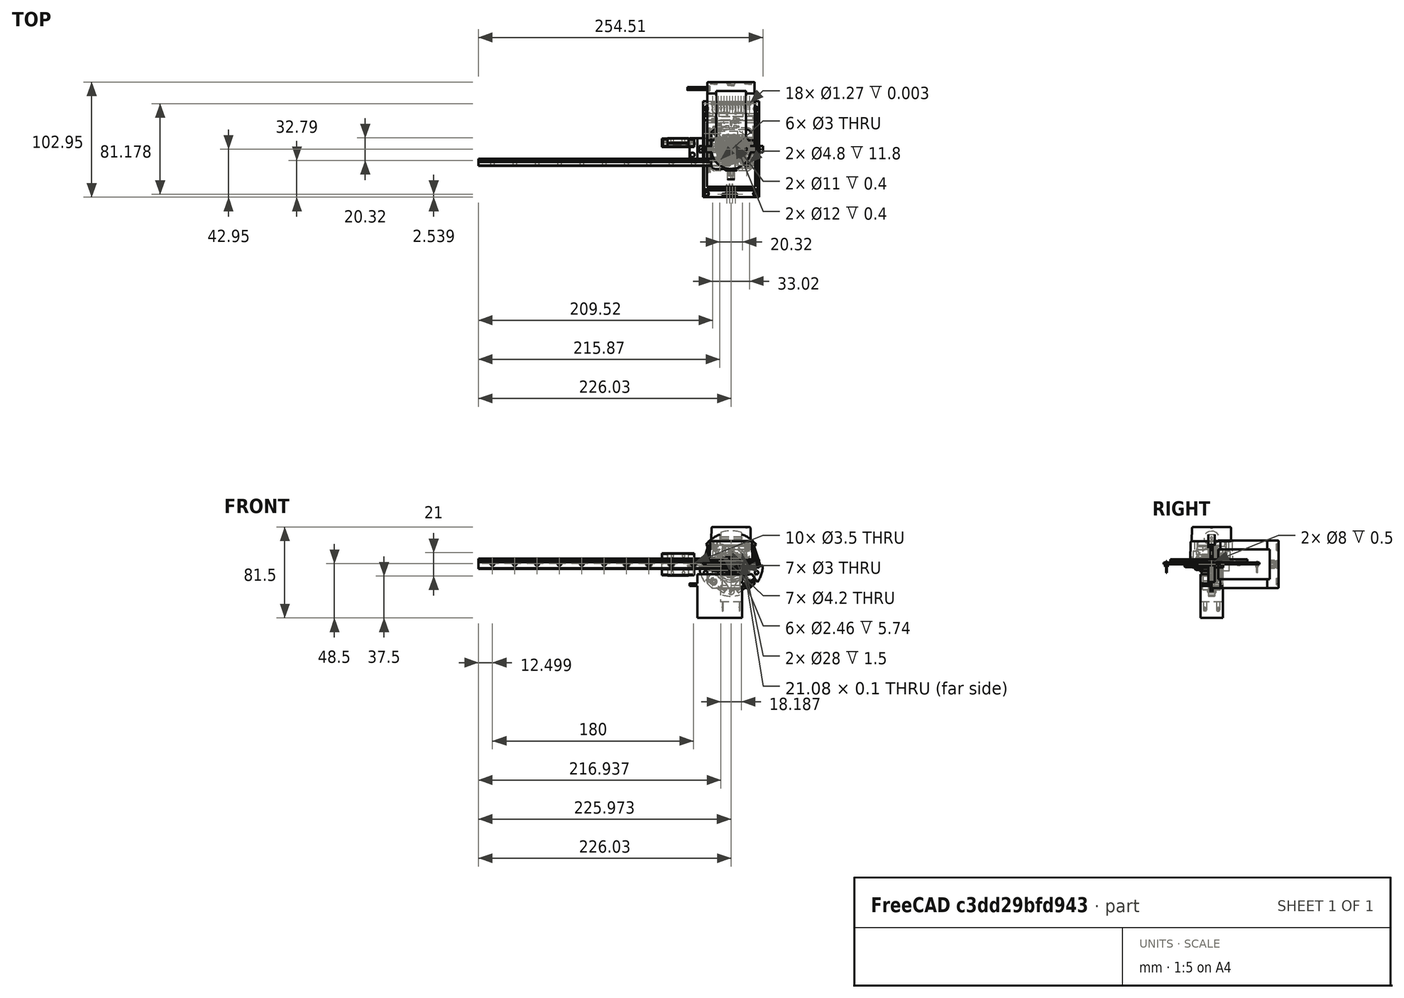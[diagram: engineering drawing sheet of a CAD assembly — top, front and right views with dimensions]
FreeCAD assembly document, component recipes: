
FREECAD ASSEMBLY — COMPONENT RECIPES ("generic-hardware")

This assembly document has 34 components, labeled P0..P33 below (a component is one placed body or linked part). 32 of them carry a construction recipe — the FreeCAD feature program that regenerates the part from scratch, quoted from this document or its linked companion documents; the rest are supplied as boundary geometry only. No exploded tour is included for this assembly.
NOTE — document 3 of 3 of this assembly tour. The two overview renders and the header above are repeated from document 1; the component sections below continue where the previous document stopped.
COMPONENT P32 — recipe-attached ("BAU-LBM4-16mm", modeled in this document).
Construction recipe (the document's own serialized feature program — sketch geometry with constraints, then the solid features built on it; lengths are millimeters unless a unit is written):

FEATURE [Sketcher::SketchObject] Sketch251
  ArcFitTolerance = 1e-06
  AttachmentSupport = -> [XZ_Plane143]
  ExternalBSplineMaxDegree = 5
  ExternalBSplineTolerance = 0.0001
  FullyConstrained = true
  InternalTolerance = 1e-06
  InvalidShape = false
  MakeInternals = false
  MapMode = 5
  Placement = pos=(0,0,0) rot=(1,0,0;1.5708rad)
  Support = -> [XZ_Plane143]
  TreeRank = 77
  ValidateShape = false
  sketch-geometry (8):
    g0: LineSegment StartX=0 StartY=6.5 StartZ=0 EndX=10.75 EndY=6.5 EndZ=0
    g1: LineSegment StartX=10.75 StartY=6.5 StartZ=0 EndX=10.75 EndY=1.5 EndZ=0
    g2: LineSegment StartX=10.75 StartY=1.5 StartZ=0 EndX=11.75 EndY=1.5 EndZ=0
    g3: LineSegment StartX=11.75 StartY=1.5 StartZ=0 EndX=11.75 EndY=0 EndZ=0
    g4: LineSegment StartX=11.75 StartY=0 StartZ=0 EndX=8 EndY=0 EndZ=0
    g5: LineSegment StartX=8 StartY=0 StartZ=0 EndX=8 EndY=-15 EndZ=0
    g6: LineSegment StartX=8 StartY=-15 StartZ=0 EndX=0 EndY=-15 EndZ=0
    g7: LineSegment StartX=0 StartY=-15 StartZ=0 EndX=0 EndY=6.5 EndZ=0
  constraints (24):
    c: PointOnObject(g0,g-2)
    c: Horizontal(g0)
    c: Coincident(g0,g1)
    c: Coincident(g1,g2)
    c: Horizontal(g2)
    c: Coincident(g2,g3)
    c: Vertical(g3)
    c: Coincident(g3,g4)
    c: Horizontal(g4)
    c: Coincident(g4,g5)
    c: Vertical(g5)
    c: Coincident(g5,g6)
    c: Horizontal(g6)
    c: Coincident(g6,g7)
    c: Coincident(g7,g0)
    c: Vertical(g7)
    c: Vertical(g1)
    c: PointOnObject(g4,g-1)
    c: DistanceX(g6,g6) = 8
    c: DistanceX(g3) = 11.75
    c: DistanceY(g3,g3) = 1.5
    c: DistanceX(g1) = 10.75
    c: DistanceY(g1,g1) = 5
    c: DistanceY(g5,g5) = 15
FEATURE [PartDesign::Revolution] Revolution
  AddSubType = 0
  Angle = 360
  Axis = (0,2e-16,1)
  Base = (0,0,0)
  ClaimChildren = false
  Fit = 0
  FitJoin = 0
  InnerFit = 0
  InnerFitJoin = 0
  InvalidShape = false
  Linearize = true
  NewSolid = false
  Profile = -> Sketch251
  ReferenceAxis = -> Sketch251 [V_Axis]
  Refine = true
  Reversed = true
  Suppress = false
  TreeRank = 78
  ValidateShape = true
  _ProfileBasedVersion = 1
FEATURE [PartDesign::Body] Body117  label="LBM4-16mm-Body"
  AutoGroupSolids = false
  ClaimAllChildren = false
  ExportMode = 0
  Group = -> [Sketch251,Revolution]
  InvalidShape = false
  Origin = -> Origin221
  Tip = -> Revolution
  TreeRank = 76
  ValidateShape = false
  _ExportChildren = -> [Revolution]
  _GroupVersion = 1
FEATURE [Sketcher::SketchObject] Sketch252
  ArcFitTolerance = 1e-06
  AttachmentSupport = -> [XZ_Plane144]
  ExternalBSplineMaxDegree = 5
  ExternalBSplineTolerance = 0.0001
  FullyConstrained = true
  InternalTolerance = 1e-06
  InvalidShape = false
  MakeInternals = false
  MapMode = 5
  Placement = pos=(0,0,0) rot=(1,0,0;1.5708rad)
  Support = -> [XZ_Plane144]
  TreeRank = 89
  ValidateShape = false
  sketch-geometry (8):
    g0: LineSegment StartX=0 StartY=10.5 StartZ=0 EndX=13 EndY=10.5 EndZ=0
    g1: LineSegment StartX=13 StartY=10.5 StartZ=0 EndX=13 EndY=8 EndZ=0
    g2: LineSegment StartX=13 StartY=8 StartZ=0 EndX=13.5 EndY=8 EndZ=0
    g3: LineSegment StartX=13.5 StartY=8 StartZ=0 EndX=13.5 EndY=3 EndZ=0
    g4: LineSegment StartX=13.5 StartY=3 StartZ=0 EndX=12.75 EndY=3 EndZ=0
    g5: LineSegment StartX=12.75 StartY=3 StartZ=0 EndX=12.75 EndY=0 EndZ=0
    g6: LineSegment StartX=12.75 StartY=0 StartZ=0 EndX=0 EndY=0 EndZ=0
    g7: LineSegment StartX=0 StartY=0 StartZ=0 EndX=0 EndY=10.5 EndZ=0
  constraints (23):
    c: PointOnObject(g0,g-2)
    c: Horizontal(g0)
    c: Coincident(g0,g1)
    c: Vertical(g1)
    c: Coincident(g1,g2)
    c: Horizontal(g2)
    c: Coincident(g2,g3)
    c: Vertical(g3)
    c: Coincident(g3,g4)
    c: Horizontal(g4)
    c: Coincident(g4,g5)
    c: PointOnObject(g5,g-1)
    c: Vertical(g5)
    c: Coincident(g5,g6)
    c: Coincident(g6,g-1)
    c: Coincident(g6,g7)
    c: Coincident(g7,g0)
    c: DistanceY(g3,g3) = 5
    c: DistanceX(g0,g0) = 13
    c: DistanceX(g2) = 13.5
    c: DistanceY(g7,g7) = 10.5
    c: DistanceY(g5,g5) = 3
    c: DistanceX(g6,g6) = 12.75
FEATURE [PartDesign::Revolution] Revolution022
  AddSubType = 0
  Angle = 360
  Axis = (0,2e-16,1)
  Base = (0,0,0)
  ClaimChildren = false
  Fit = 0
  FitJoin = 0
  InnerFit = 0
  InnerFitJoin = 0
  InvalidShape = false
  Linearize = true
  NewSolid = false
  Profile = -> Sketch252
  ReferenceAxis = -> Sketch252 [V_Axis]
  Refine = true
  Reversed = true
  Suppress = false
  TreeRank = 90
  ValidateShape = true
  _ProfileBasedVersion = 1
FEATURE [PartDesign::Fillet] Fillet049
  AddSubType = 0
  Base = -> Revolution022 [Edge1]
  BaseFeature = -> Revolution022
  InvalidShape = false
  NewSolid = false
  Radius = 2
  Refine = true
  SupportTransform = false
  Suppress = false
  TreeRank = 91
  UseAllEdges = false
  ValidateShape = true
FEATURE [PartDesign::Chamfer] Chamfer058
  AddSubType = 0
  Angle = 45
  Base = -> Fillet049 [Edge6,Edge8]
  BaseFeature = -> Fillet049
  ChamferType = 0
  FlipDirection = false
  InvalidShape = false
  NewSolid = false
  Refine = true
  Size = 0.4
  Size2 = 1
  SupportTransform = false
  Suppress = false
  TreeRank = 92
  UseAllEdges = false
  ValidateShape = true
FEATURE [PartDesign::Fillet] Fillet050
  AddSubType = 0
  Base = -> Chamfer058 [Edge15]
  BaseFeature = -> Chamfer058
  InvalidShape = false
  NewSolid = false
  Radius = 0.2
  Refine = true
  SupportTransform = false
  Suppress = false
  TreeRank = 93
  UseAllEdges = false
  ValidateShape = true
FEATURE [PartDesign::Body] Body118  label="LBM4-Button"
  AutoGroupSolids = false
  ClaimAllChildren = false
  ExportMode = 0
  Group = -> [Sketch252,Revolution022,Fillet049,Chamfer058,Fillet050]
  InvalidShape = false
  Origin = -> Origin222
  Placement = pos=(0,0,5.5) rot=(0,0,1;0rad)
  Tip = -> Fillet050
  TreeRank = 88
  ValidateShape = false
  _ExportChildren = -> [Revolution022,Fillet049,Chamfer058,Fillet050]
  _GroupVersion = 1
FEATURE [Sketcher::SketchObject] Sketch253
  ArcFitTolerance = 1e-06
  AttachmentSupport = -> [XZ_Plane145]
  ExternalBSplineMaxDegree = 5
  ExternalBSplineTolerance = 0.0001
  FullyConstrained = true
  InternalTolerance = 1e-06
  InvalidShape = false
  MakeInternals = false
  MapMode = 5
  Placement = pos=(0,0,0) rot=(1,0,0;1.5708rad)
  Support = -> [XZ_Plane145]
  TreeRank = 104
  ValidateShape = false
  sketch-geometry (1):
    g0: Circle CenterX=8.5 CenterY=0 CenterZ=0 NormalX=0 NormalY=0 NormalZ=1 AngleXU=0 Radius=0.75
  constraints (3):
    c: PointOnObject(g0,g-1)
    c: Diameter(g0) = 1.5
    c: DistanceX(g0) = 8.5
FEATURE [PartDesign::Revolution] Revolution023
  AddSubType = 0
  Angle = 360
  Axis = (0,2e-16,1)
  Base = (0,0,0)
  ClaimChildren = false
  Fit = 0
  FitJoin = 0
  InnerFit = 0
  InnerFitJoin = 0
  InvalidShape = false
  Linearize = true
  NewSolid = false
  Profile = -> Sketch253
  ReferenceAxis = -> Sketch253 [V_Axis]
  Refine = true
  Reversed = true
  Suppress = false
  TreeRank = 105
  ValidateShape = true
  _ProfileBasedVersion = 1
FEATURE [PartDesign::Body] Body119  label="LBM4-Joint"
  AutoGroupSolids = false
  ClaimAllChildren = false
  ExportMode = 0
  Group = -> [Sketch253,Revolution023]
  InvalidShape = false
  Origin = -> Origin223
  Placement = pos=(0,0,-0.7) rot=(0,0,1;0rad)
  Tip = -> Revolution023
  TreeRank = 103
  ValidateShape = false
  _ExportChildren = -> [Revolution023]
  _GroupVersion = 1
FEATURE [PartDesign::SubShapeBinder] Pad101_Profile  label="Pad101_Profile(Revolution)"
  BindCopyOnChange = 0
  BindMode = 0
  ClaimChildren = false
  Context = -> Group008 [Part050.Body120.Pad101_Profile.]
  EdgeTolerance = 1e-06
  FillStyle = 0
  Fuse = false
  InvalidShape = false
  MakeFace = true
  MergeEdges = true
  OffsetFill = false
  OffsetIntersection = false
  OffsetJoinType = 0
  OffsetOpenResult = false
  Outline = false
  PartialLoad = false
  Relative = true
  SplitEdges = false
  Support = -> [Revolution[Face7]]
  TightBound = false
  TreeRank = 117
  ValidateShape = false
  _Version = 8
FEATURE [PartDesign::Pad] Pad101
  AddSubType = 0
  AlongSketchNormal = false
  AutoTaperInnerAngle = true
  CheckUpToFaceLimits = true
  ClaimChildren = false
  Direction = (0,-2e-16,-1)
  Fit = 0
  FitJoin = 0
  InnerFit = 0
  InnerFitJoin = 0
  InvalidShape = false
  Length = 8
  Length2 = 10
  Linearize = true
  NewSolid = false
  Profile = -> Pad101_Profile
  Refine = true
  Suppress = false
  TaperInnerAngle = 0
  TaperInnerAngleRev = 0
  TreeRank = 118
  Type = 0
  ValidateShape = true
  _ProfileBasedVersion = 1
FEATURE [PartDesign::Body] Body120  label="LBM4-CapsuleConnecteur"
  AutoGroupSolids = false
  ClaimAllChildren = false
  ExportMode = 0
  Group = -> [Pad101,Pad101_Profile]
  InvalidShape = false
  Origin = -> Origin224
  Tip = -> Pad101
  TreeRank = 115
  ValidateShape = false
  _ExportChildren = -> [Pad101]
  _GroupVersion = 1
FEATURE [Sketcher::SketchObject] Sketch254
  ArcFitTolerance = 1e-06
  AttachmentSupport = -> [XY_Plane147]
  ExternalBSplineMaxDegree = 5
  ExternalBSplineTolerance = 0.0001
  FullyConstrained = true
  InternalTolerance = 1e-06
  InvalidShape = false
  MakeInternals = false
  MapMode = 5
  Support = -> [XY_Plane147]
  TreeRank = 129
  ValidateShape = false
  sketch-geometry (8):
    g0: LineSegment StartX=10.9697 StartY=0 StartZ=0 EndX=5.48483 EndY=9.5 EndZ=0
    g1: LineSegment StartX=5.48483 StartY=9.5 StartZ=0 EndX=-5.48483 EndY=9.5 EndZ=0
    g2: LineSegment StartX=-5.48483 StartY=9.5 StartZ=0 EndX=-10.9697 EndY=-1.8e-15 EndZ=0
    g3: LineSegment StartX=-10.9697 StartY=-1.3e-15 StartZ=0 EndX=-5.48483 EndY=-9.5 EndZ=0
    g4: LineSegment StartX=-5.48483 StartY=-9.5 StartZ=0 EndX=5.48483 EndY=-9.5 EndZ=0
    g5: LineSegment StartX=5.48483 StartY=-9.5 StartZ=0 EndX=10.9697 EndY=0 EndZ=0
    g6: Circle [constr] CenterX=0 CenterY=0 CenterZ=0 NormalX=0 NormalY=0 NormalZ=1 AngleXU=0 Radius=10.9697
    g7: Circle CenterX=0 CenterY=0 CenterZ=0 NormalX=0 NormalY=0 NormalZ=1 AngleXU=0 Radius=7.5
  constraints (18):
    c: Coincident(g0,g1)
    c: Coincident(g1,g2)
    c: Coincident(g2,g3)
    c: Coincident(g3,g4)
    c: Coincident(g4,g5)
    c: Coincident(g5,g0)
    c: Equal(g0, g1-g5) x5
    c: PointOnObject(g0,g6)
    c: PointOnObject(g1,g6)
    c: PointOnObject(g2,g6)
    c: PointOnObject(g3,g6)
    c: PointOnObject(g4,g6)
    c: PointOnObject(g5,g6)
    c: Coincident(g6,g-1)
    c: PointOnObject(g5,g-1)
    c: DistanceY(g4,g0) = 19
    c: Coincident(g7,g6)
    c: Diameter(g7) = 15
FEATURE [PartDesign::Pad] Pad102
  AddSubType = 0
  AlongSketchNormal = false
  AutoTaperInnerAngle = true
  CheckUpToFaceLimits = true
  ClaimChildren = false
  Direction = (0,0,1)
  Fit = 0
  FitJoin = 0
  InnerFit = 0
  InnerFitJoin = 0
  InvalidShape = false
  Length = 2.8
  Length2 = 10
  Linearize = true
  Midplane = true
  NewSolid = false
  Profile = -> Sketch254
  ReferenceAxis = -> Sketch254 [N_Axis]
  Refine = true
  Suppress = false
  TaperInnerAngle = 0
  TaperInnerAngleRev = 0
  TreeRank = 130
  Type = 0
  ValidateShape = true
  _ProfileBasedVersion = 1
FEATURE [PartDesign::Fillet] Fillet051
  AddSubType = 0
  Base = -> Pad102 [Edge1,Edge14,Edge2,Edge5,Edge8,Edge11]
  BaseFeature = -> Pad102
  InvalidShape = false
  NewSolid = false
  Radius = 0.6
  Refine = true
  SupportTransform = false
  Suppress = false
  TreeRank = 132
  UseAllEdges = false
  ValidateShape = true
FEATURE [Sketcher::SketchObject] Sketch255
  ArcFitTolerance = 1e-06
  AttachmentSupport = -> [XZ_Plane147]
  ExternalBSplineMaxDegree = 5
  ExternalBSplineTolerance = 0.0001
  FullyConstrained = false
  InternalTolerance = 1e-06
  InvalidShape = false
  MakeInternals = false
  MapMode = 5
  Placement = pos=(0,0,0) rot=(1,0,0;1.5708rad)
  Support = -> [XZ_Plane147]
  TreeRank = 133
  ValidateShape = false
  sketch-geometry (3):
    g0: LineSegment StartX=8.99798 StartY=1.52118 StartZ=0 EndX=10.9649 EndY=0.806128 EndZ=0
    g1: LineSegment StartX=10.9649 StartY=0.806128 StartZ=0 EndX=10.9649 EndY=1.52118 EndZ=0
    g2: LineSegment StartX=10.9649 StartY=1.52118 StartZ=0 EndX=8.99798 EndY=1.52118 EndZ=0
  constraints (5):
    c: Coincident(g0,g1)
    c: Vertical(g1)
    c: Coincident(g1,g2)
    c: Coincident(g2,g0)
    c: Horizontal(g2)
FEATURE [PartDesign::Groove] Groove005
  AddSubType = 1
  Angle = 360
  Axis = (0,2e-16,1)
  Base = (0,0,0)
  BaseFeature = -> Fillet051
  ClaimChildren = false
  Fit = 0
  FitJoin = 0
  InnerFit = 0
  InnerFitJoin = 0
  InvalidShape = false
  Linearize = true
  NewSolid = false
  Profile = -> Sketch255
  ReferenceAxis = -> Sketch255 [V_Axis]
  Refine = true
  Suppress = false
  TreeRank = 134
  ValidateShape = true
  _ProfileBasedVersion = 1
FEATURE [PartDesign::Mirrored] Mirrored
  AddSubType = 0
  BaseFeature = -> Groove005
  CopyShape = false
  InvalidShape = false
  MirrorPlane = -> XY_Plane147
  NewSolid = false
  OriginalSubs = -> [Groove005]
  Originals = -> [Groove005]
  ParallelTransform = true
  Refine = true
  SubTransform = true
  Suppress = false
  TreeRank = 135
  ValidateShape = true
  _Version = 4
FEATURE [PartDesign::Body] Body121  label="LBM4-Ecrou"
  AutoGroupSolids = false
  ClaimAllChildren = false
  ExportMode = 0
  Group = -> [Sketch254,Pad102,Fillet051,Sketch255,Groove005,Mirrored]
  InvalidShape = false
  Origin = -> Origin225
  Placement = pos=(0,0,-4.5) rot=(0,0,1;0rad)
  Tip = -> Mirrored
  TreeRank = 128
  ValidateShape = false
  _ExportChildren = -> [Pad102,Fillet051,Groove005,Mirrored]
  _GroupVersion = 1
COMPONENT P33 — recipe-attached ("SuctionCupAdaptator", modeled in this document).
Construction recipe (the document's own serialized feature program — sketch geometry with constraints, then the solid features built on it; lengths are millimeters unless a unit is written):

FEATURE [Sketcher::SketchObject] Sketch256
  ArcFitTolerance = 1e-06
  AttachmentSupport = -> [XY_Plane148]
  ExternalBSplineMaxDegree = 5
  ExternalBSplineTolerance = 0.0001
  FixShape = 1
  FullyConstrained = true
  InternalTolerance = 1e-06
  InvalidShape = false
  MakeInternals = false
  MapMode = 5
  Support = -> [XY_Plane148]
  TreeRank = 148
  ValidateShape = false
  sketch-geometry (7):
    g0: LineSegment StartX=0 StartY=-6.9282 StartZ=0 EndX=6 EndY=-3.4641 EndZ=0
    g1: LineSegment StartX=6 StartY=-3.4641 StartZ=0 EndX=6 EndY=3.4641 EndZ=0
    g2: LineSegment StartX=6 StartY=3.4641 StartZ=0 EndX=0 EndY=6.9282 EndZ=0
    g3: LineSegment StartX=1e-16 StartY=6.9282 StartZ=0 EndX=-6 EndY=3.4641 EndZ=0
    g4: LineSegment StartX=-6 StartY=3.4641 StartZ=0 EndX=-6 EndY=-3.4641 EndZ=0
    g5: LineSegment StartX=-6 StartY=-3.4641 StartZ=0 EndX=0 EndY=-6.9282 EndZ=0
    g6: Circle [constr] CenterX=0 CenterY=0 CenterZ=0 NormalX=0 NormalY=0 NormalZ=1 AngleXU=0 Radius=6.9282
  constraints (16):
    c: Coincident(g0,g1)
    c: Coincident(g1,g2)
    c: Coincident(g2,g3)
    c: Coincident(g3,g4)
    c: Coincident(g4,g5)
    c: Coincident(g5,g0)
    c: Equal(g0, g1-g5) x5
    c: PointOnObject(g0,g6)
    c: PointOnObject(g1,g6)
    c: PointOnObject(g2,g6)
    c: PointOnObject(g3,g6)
    c: PointOnObject(g4,g6)
    c: PointOnObject(g5,g6)
    c: Coincident(g6,g-1)
    c: PointOnObject(g5,g-2)
    c: DistanceX(g3,g1) = 12
FEATURE [PartDesign::Pad] Pad103
  AddSubType = 0
  AlongSketchNormal = false
  AutoTaperInnerAngle = true
  CheckUpToFaceLimits = true
  ClaimChildren = false
  Direction = (0,0,1)
  Fit = 0
  FitJoin = 0
  FixShape = 1
  InnerFit = 0
  InnerFitJoin = 0
  InvalidShape = false
  Length = 8
  Length2 = 10
  Linearize = true
  NewSolid = false
  Profile = -> Sketch256
  ReferenceAxis = -> Sketch256 [N_Axis]
  Refine = true
  Suppress = false
  TaperInnerAngle = 0
  TaperInnerAngleRev = 0
  TreeRank = 149
  Type = 0
  ValidateShape = true
  _ProfileBasedVersion = 1
FEATURE [Sketcher::SketchObject] Sketch257
  ArcFitTolerance = 1e-06
  AttachmentSupport = -> [YZ_Plane148]
  ExternalBSplineMaxDegree = 5
  ExternalBSplineTolerance = 0.0001
  FixShape = 1
  FullyConstrained = true
  InternalTolerance = 1e-06
  InvalidShape = false
  MakeInternals = false
  MapMode = 5
  Placement = pos=(0,0,0) rot=(0.57735,0.57735,0.57735;2.0944rad)
  Support = -> [YZ_Plane148]
  TreeRank = 150
  ValidateShape = false
  sketch-geometry (6):
    g0: LineSegment StartX=0 StartY=0 StartZ=0 EndX=2.5 EndY=0 EndZ=0
    g1: LineSegment StartX=2.5 StartY=0 StartZ=0 EndX=2.5 EndY=-3 EndZ=0
    g2: LineSegment StartX=2.5 StartY=-3 StartZ=0 EndX=3.5 EndY=-3 EndZ=0
    g3: LineSegment StartX=3.5 StartY=-3 StartZ=0 EndX=3.5 EndY=-5.4 EndZ=0
    g4: LineSegment StartX=3.5 StartY=-5.4 StartZ=0 EndX=0 EndY=-5.4 EndZ=0
    g5: LineSegment StartX=0 StartY=-5.4 StartZ=0 EndX=0 EndY=0 EndZ=0
  constraints (17):
    c: Coincident(g-1,g0)
    c: PointOnObject(g0,g-1)
    c: Coincident(g0,g1)
    c: Vertical(g1)
    c: Coincident(g1,g2)
    c: Horizontal(g2)
    c: Coincident(g2,g3)
    c: Vertical(g3)
    c: Coincident(g3,g4)
    c: PointOnObject(g4,g-2)
    c: Horizontal(g4)
    c: Coincident(g4,g5)
    c: Coincident(g5,g0)
    c: DistanceX(g0,g0) = 2.5
    c: DistanceX(g4,g4) = 3.5
    c: DistanceY(g1,g1) = 3
    c: DistanceY(g3,g0) = 5.4
FEATURE [PartDesign::Revolution] Revolution024
  AddSubType = 0
  Angle = 360
  Axis = (-2e-16,3e-16,1)
  Base = (0,0,0)
  BaseFeature = -> Pad103
  ClaimChildren = false
  Fit = 0
  FitJoin = 0
  FixShape = 1
  InnerFit = 0
  InnerFitJoin = 0
  InvalidShape = false
  Linearize = true
  NewSolid = false
  Profile = -> Sketch257
  ReferenceAxis = -> Sketch257 [V_Axis]
  Refine = true
  Reversed = true
  Suppress = false
  TreeRank = 151
  ValidateShape = true
  _ProfileBasedVersion = 1
FEATURE [Sketcher::SketchObject] Sketch258
  ArcFitTolerance = 1e-06
  AttachmentSupport = -> [XZ_Plane148]
  ExternalBSplineMaxDegree = 5
  ExternalBSplineTolerance = 0.0001
  ExternalGeometry = -> [Revolution024]
  FixShape = 1
  FullyConstrained = true
  InternalTolerance = 1e-06
  InvalidShape = false
  MakeInternals = false
  MapMode = 5
  Placement = pos=(0,0,0) rot=(1,0,0;1.5708rad)
  Support = -> [XZ_Plane148]
  TreeRank = 152
  ValidateShape = false
  sketch-geometry (6):
    g0: LineSegment StartX=0 StartY=8 StartZ=0 EndX=0 EndY=16 EndZ=0
    g1: LineSegment StartX=0 StartY=16 StartZ=0 EndX=2.5 EndY=16 EndZ=0
    g2: LineSegment StartX=2.5 StartY=16 StartZ=0 EndX=2.5 EndY=10 EndZ=0
    g3: LineSegment StartX=2.5 StartY=10 StartZ=0 EndX=1.75 EndY=10 EndZ=0
    g4: LineSegment StartX=1.75 StartY=10 StartZ=0 EndX=1.75 EndY=8 EndZ=0
    g5: LineSegment StartX=1.75 StartY=8 StartZ=0 EndX=0 EndY=8 EndZ=0
  constraints (18):
    c: PointOnObject(g0,g-2)
    c: PointOnObject(g0,g-2)
    c: Coincident(g0,g1)
    c: Horizontal(g1)
    c: Coincident(g1,g2)
    c: Coincident(g2,g3)
    c: Horizontal(g3)
    c: Coincident(g3,g4)
    c: Vertical(g4)
    c: Coincident(g4,g5)
    c: Coincident(g5,g0)
    c: Horizontal(g5)
    c: Vertical(g2)
    c: PointOnObject(g4,g-3)
    c: DistanceX(g1,g1) = 2.5
    c: DistanceX(g5,g5) = 1.75
    c: DistanceY(g0,g0) = 8
    c: DistanceY(g2,g2) = 6
FEATURE [PartDesign::Revolution] Revolution025
  AddSubType = 0
  Angle = 360
  Axis = (0,2e-16,1)
  Base = (0,0,0)
  BaseFeature = -> Revolution024
  ClaimChildren = false
  Fit = 0
  FitJoin = 0
  FixShape = 1
  InnerFit = 0
  InnerFitJoin = 0
  InvalidShape = false
  Linearize = true
  NewSolid = false
  Profile = -> Sketch258
  ReferenceAxis = -> Sketch258 [V_Axis]
  Refine = true
  Reversed = true
  Suppress = false
  TreeRank = 153
  ValidateShape = true
  _ProfileBasedVersion = 1
FEATURE [PartDesign::Chamfer] Chamfer059
  AddSubType = 0
  Angle = 45
  Base = -> Revolution025 [Edge26,Edge29]
  BaseFeature = -> Revolution025
  ChamferType = 0
  FixShape = 1
  FlipDirection = false
  InvalidShape = false
  NewSolid = false
  Refine = true
  Size = 0.5
  Size2 = 1
  SupportTransform = false
  Suppress = false
  TreeRank = 154
  UseAllEdges = false
  ValidateShape = true
FEATURE [Sketcher::SketchObject] Sketch259
  ArcFitTolerance = 1e-06
  AttachmentSupport = -> [Chamfer059]
  ExternalBSplineMaxDegree = 5
  ExternalBSplineTolerance = 0.0001
  FixShape = 1
  FullyConstrained = true
  InternalTolerance = 1e-06
  InvalidShape = false
  MakeInternals = false
  MapMode = 5
  Placement = pos=(1.2e-15,-1.5e-15,-5.4) rot=(1,0,0;3.14159rad)
  Support = -> [Chamfer059]
  TreeRank = 155
  ValidateShape = false
  sketch-geometry (1):
    g0: Circle CenterX=0 CenterY=0 CenterZ=0 NormalX=0 NormalY=0 NormalZ=1 AngleXU=0 Radius=1.5
  constraints (2):
    c: Coincident(g0,g-1)
    c: Diameter(g0) = 3
FEATURE [PartDesign::Pocket] Pocket087
  AddSubType = 1
  AlongSketchNormal = false
  AutoTaperInnerAngle = true
  BaseFeature = -> Chamfer059
  CheckUpToFaceLimits = true
  ClaimChildren = false
  Direction = (-2e-16,3e-16,1)
  Fit = 0
  FitJoin = 0
  FixShape = 1
  InnerFit = 0
  InnerFitJoin = 0
  InvalidShape = false
  Length = 12
  Length2 = 10
  Linearize = true
  NewSolid = false
  Profile = -> Sketch259
  ReferenceAxis = -> Sketch259 [N_Axis]
  Refine = true
  Suppress = false
  TaperInnerAngle = 0
  TaperInnerAngleRev = 0
  TreeRank = 156
  Type = 0
  ValidateShape = true
  _ProfileBasedVersion = 1
  _Version = 1
FEATURE [Sketcher::SketchObject] Sketch260
  ArcFitTolerance = 1e-06
  AttachmentSupport = -> [YZ_Plane148]
  ExternalBSplineMaxDegree = 5
  ExternalBSplineTolerance = 0.0001
  FixShape = 1
  FullyConstrained = true
  InternalTolerance = 1e-06
  InvalidShape = false
  MakeInternals = false
  MapMode = 5
  Placement = pos=(0,0,0) rot=(0.57735,0.57735,0.57735;2.0944rad)
  Support = -> [YZ_Plane148]
  TreeRank = 157
  ValidateShape = false
  sketch-geometry (1):
    g0: Circle CenterX=0 CenterY=4 CenterZ=0 NormalX=0 NormalY=0 NormalZ=1 AngleXU=0 Radius=2.5
  constraints (3):
    c: PointOnObject(g0,g-2)
    c: Diameter(g0) = 5
    c: DistanceY(g-1,g0) = 4
FEATURE [PartDesign::Pocket] Pocket088
  AddSubType = 1
  AlongSketchNormal = false
  AutoTaperInnerAngle = true
  BaseFeature = -> Pocket087
  CheckUpToFaceLimits = true
  ClaimChildren = false
  Direction = (-1,2e-16,-3e-16)
  Fit = 0
  FitJoin = 0
  FixShape = 1
  InnerFit = 0
  InnerFitJoin = 0
  InvalidShape = false
  Length = 5
  Length2 = 10
  Linearize = true
  Midplane = true
  NewSolid = false
  Profile = -> Sketch260
  ReferenceAxis = -> Sketch260 [N_Axis]
  Refine = true
  Suppress = false
  TaperInnerAngle = 0
  TaperInnerAngleRev = 0
  TreeRank = 158
  Type = 1
  ValidateShape = true
  _ProfileBasedVersion = 1
  _Version = 1
FEATURE [PartDesign::Chamfer] Chamfer060
  AddSubType = 0
  Angle = 45
  Base = -> Pocket088 [Edge24,Edge27]
  BaseFeature = -> Pocket088
  ChamferType = 0
  FixShape = 1
  FlipDirection = false
  InvalidShape = false
  NewSolid = false
  Refine = true
  Size = 0.2
  Size2 = 1
  SupportTransform = false
  Suppress = false
  TreeRank = 159
  UseAllEdges = false
  ValidateShape = true
FEATURE [PartDesign::Fillet] Fillet052
  AddSubType = 0
  Base = -> Chamfer060 [Edge2,Edge5,Edge8,Edge26,Edge28,Edge21]
  BaseFeature = -> Chamfer060
  FixShape = 1
  InvalidShape = false
  NewSolid = false
  Radius = 0.4
  Refine = true
  SupportTransform = false
  Suppress = false
  TreeRank = 160
  UseAllEdges = false
  ValidateShape = true
FEATURE [PartDesign::Body] Body122  label="Adaptator-suction-cup-M5-VM"
  AutoGroupSolids = false
  ClaimAllChildren = false
  ExportMode = 0
  FixShape = 1
  Group = -> [Sketch256,Pad103,Sketch257,Revolution024,Sketch258,Revolution025,Chamfer059,Sketch259,Pocket087,Sketch260,Pocket088,Chamfer060,Fillet052]
  InvalidShape = false
  Origin = -> Origin226
  SingleSolid = true
  Tip = -> Fillet052
  TreeRank = 146
  ValidateShape = false
  _ExportChildren = -> [Pad103,Revolution024,Revolution025,Chamfer059,Pocket087,Pocket088,Chamfer060,Fillet052]
  _GroupVersion = 1
FEATURE [Sketcher::SketchObject] Sketch261
  ArcFitTolerance = 1e-06
  AttachmentSupport = -> [YZ_Plane149]
  ExternalBSplineMaxDegree = 5
  ExternalBSplineTolerance = 0.0001
  FixShape = 1
  FullyConstrained = true
  InternalTolerance = 1e-06
  InvalidShape = false
  MakeInternals = false
  MapMode = 5
  Placement = pos=(0,0,0) rot=(0.57735,0.57735,0.57735;2.0944rad)
  Support = -> [YZ_Plane149]
  TreeRank = 174
  ValidateShape = false
  sketch-geometry (8):
    g0: LineSegment StartX=3.57957 StartY=0 StartZ=0 EndX=1.78979 EndY=3.1 EndZ=0
    g1: LineSegment StartX=1.78979 StartY=3.1 StartZ=0 EndX=-1.78979 EndY=3.1 EndZ=0
    g2: LineSegment StartX=-1.78979 StartY=3.1 StartZ=0 EndX=-3.57957 EndY=6.26e-14 EndZ=0
    g3: LineSegment StartX=-3.57957 StartY=6.27e-14 StartZ=0 EndX=-1.78979 EndY=-3.1 EndZ=0
    g4: LineSegment StartX=-1.78979 StartY=-3.1 StartZ=0 EndX=1.78979 EndY=-3.1 EndZ=0
    g5: LineSegment StartX=1.78979 StartY=-3.1 StartZ=0 EndX=3.57957 EndY=0 EndZ=0
    g6: Circle [constr] CenterX=0 CenterY=0 CenterZ=0 NormalX=0 NormalY=0 NormalZ=1 AngleXU=0 Radius=3.57957
    g7: Circle CenterX=0 CenterY=0 CenterZ=0 NormalX=0 NormalY=0 NormalZ=1 AngleXU=0 Radius=1.5
  constraints (18):
    c: Coincident(g0,g1)
    c: Coincident(g1,g2)
    c: Coincident(g2,g3)
    c: Coincident(g3,g4)
    c: Coincident(g4,g5)
    c: Coincident(g5,g0)
    c: Equal(g0, g1-g5) x5
    c: PointOnObject(g0,g6)
    c: PointOnObject(g1,g6)
    c: PointOnObject(g2,g6)
    c: PointOnObject(g3,g6)
    c: PointOnObject(g4,g6)
    c: PointOnObject(g5,g6)
    c: Coincident(g6,g-1)
    c: PointOnObject(g5,g-1)
    c: DistanceY(g4,g0) = 6.2
    c: Coincident(g7,g6)
    c: Diameter(g7) = 3
FEATURE [PartDesign::Pad] Pad104
  AddSubType = 0
  AlongSketchNormal = false
  AutoTaperInnerAngle = true
  CheckUpToFaceLimits = true
  ClaimChildren = false
  Direction = (1,-2e-16,3e-16)
  Fit = 0
  FitJoin = 0
  FixShape = 1
  InnerFit = 0
  InnerFitJoin = 0
  InvalidShape = false
  Length = 2.5
  Length2 = 10
  Linearize = true
  NewSolid = false
  Profile = -> Sketch261
  ReferenceAxis = -> Sketch261 [N_Axis]
  Refine = true
  Suppress = false
  TaperInnerAngle = 0
  TaperInnerAngleRev = 0
  TreeRank = 175
  Type = 0
  ValidateShape = true
  _ProfileBasedVersion = 1
FEATURE [Sketcher::SketchObject] Sketch262
  ArcFitTolerance = 1e-06
  AttachmentSupport = -> [XZ_Plane149]
  ExternalBSplineMaxDegree = 5
  ExternalBSplineTolerance = 0.0001
  FixShape = 1
  FullyConstrained = true
  InternalTolerance = 1e-06
  InvalidShape = false
  MakeInternals = false
  MapMode = 5
  Placement = pos=(0,0,0) rot=(1,0,0;1.5708rad)
  Support = -> [XZ_Plane149]
  TreeRank = 176
  ValidateShape = false
  sketch-geometry (11):
    g0: LineSegment [constr] StartX=10 StartY=-2.25 StartZ=0 EndX=0 EndY=-2.25 EndZ=0
    g1: LineSegment StartX=0 StartY=-2.25 StartZ=0 EndX=0 EndY=-1.5 EndZ=0
    g2: LineSegment StartX=0 StartY=-1.5 StartZ=0 EndX=10 EndY=-1.5 EndZ=0
    g3: LineSegment StartX=10 StartY=-1.5 StartZ=0 EndX=10 EndY=-2.25 EndZ=0
    g4: LineSegment StartX=10 StartY=-2.25 StartZ=0 EndX=7.8 EndY=-2.5 EndZ=0
    g5: LineSegment StartX=7.8 StartY=-2.5 StartZ=0 EndX=7 EndY=-2.5 EndZ=0
    g6: LineSegment StartX=7 StartY=-2.5 StartZ=0 EndX=7 EndY=-2.25 EndZ=0
    g7: LineSegment StartX=7 StartY=-2.25 StartZ=0 EndX=4.8 EndY=-2.5 EndZ=0
    g8: LineSegment StartX=4.8 StartY=-2.5 StartZ=0 EndX=4 EndY=-2.5 EndZ=0
    g9: LineSegment StartX=4 StartY=-2.5 StartZ=0 EndX=4 EndY=-2.25 EndZ=0
    g10: LineSegment StartX=0 StartY=-2.25 StartZ=0 EndX=4 EndY=-2.25 EndZ=0
  constraints (32):
    c: PointOnObject(g0,g-2)
    c: Horizontal(g0)
    c: DistanceX(g0,g0) = 10
    c: Coincident(g0,g1)
    c: PointOnObject(g1,g-2)
    c: Coincident(g1,g2)
    c: Horizontal(g2)
    c: Coincident(g2,g3)
    c: Coincident(g3,g0)
    c: Vertical(g3)
    c: DistanceY(g0) = -2.25
    c: DistanceY(g2,g-1) = 1.5
    c: Coincident(g0,g4)
    c: Coincident(g4,g5)
    c: Horizontal(g5)
    c: Coincident(g5,g6)
    c: PointOnObject(g6,g0)
    c: Coincident(g6,g7)
    c: Coincident(g7,g8)
    c: Horizontal(g8)
    c: Coincident(g8,g9)
    c: PointOnObject(g9,g0)
    c: Vertical(g9)
    c: Vertical(g6)
    c: Equal(g5,g8)
    c: Equal(g6,g9)
    c: Equal(g7,g4)
    c: DistanceX(g6,g3) = 3
    c: DistanceY(g5,g-1) = 2.5
    c: DistanceX(g5,g5) = 0.8
    c: Coincident(g10,g1)
    c: Coincident(g10,g9)
FEATURE [PartDesign::Revolution] Revolution026
  AddSubType = 0
  Angle = 360
  Axis = (1,0,0)
  Base = (0,0,0)
  BaseFeature = -> Pad104
  ClaimChildren = false
  Fit = 0
  FitJoin = 0
  FixShape = 1
  InnerFit = 0
  InnerFitJoin = 0
  InvalidShape = false
  Linearize = true
  NewSolid = false
  Profile = -> Sketch262
  ReferenceAxis = -> Sketch262 [H_Axis]
  Refine = true
  Reversed = true
  Suppress = false
  TreeRank = 177
  ValidateShape = true
  _ProfileBasedVersion = 1
FEATURE [Sketcher::SketchObject] Sketch263
  ArcFitTolerance = 1e-06
  AttachmentSupport = -> [XZ_Plane149]
  ExternalBSplineMaxDegree = 5
  ExternalBSplineTolerance = 0.0001
  FixShape = 1
  FullyConstrained = true
  InternalTolerance = 1e-06
  InvalidShape = false
  MakeInternals = false
  MapMode = 5
  Placement = pos=(0,0,0) rot=(1,0,0;1.5708rad)
  Support = -> [XZ_Plane149]
  TreeRank = 178
  ValidateShape = false
  sketch-geometry (6):
    g0: LineSegment StartX=0 StartY=1.5 StartZ=0 EndX=-4.5 EndY=1.5 EndZ=0
    g1: LineSegment StartX=-4.5 StartY=1.5 StartZ=0 EndX=-4.5 EndY=2.5 EndZ=0
    g2: LineSegment StartX=-4.5 StartY=2.5 StartZ=0 EndX=-1.5 EndY=2.5 EndZ=0
    g3: LineSegment StartX=-1.5 StartY=2.5 StartZ=0 EndX=-1.5 EndY=2 EndZ=0
    g4: LineSegment StartX=-1.5 StartY=2 StartZ=0 EndX=0 EndY=2 EndZ=0
    g5: LineSegment StartX=0 StartY=2 StartZ=0 EndX=0 EndY=1.5 EndZ=0
  constraints (18):
    c: PointOnObject(g0,g-2)
    c: Horizontal(g0)
    c: Coincident(g0,g1)
    c: Vertical(g1)
    c: Coincident(g1,g2)
    c: Horizontal(g2)
    c: Coincident(g2,g3)
    c: Vertical(g3)
    c: Coincident(g3,g4)
    c: PointOnObject(g4,g-2)
    c: Horizontal(g4)
    c: Coincident(g4,g5)
    c: Coincident(g5,g0)
    c: DistanceY(g1) = 2.5
    c: DistanceY(g0) = 1.5
    c: DistanceY(g4) = 2
    c: DistanceX(g2,g2) = 3
    c: DistanceX(g0,g0) = 4.5
FEATURE [PartDesign::Revolution] Revolution027
  AddSubType = 0
  Angle = 360
  Axis = (1,0,0)
  Base = (0,0,0)
  BaseFeature = -> Revolution026
  ClaimChildren = false
  Fit = 0
  FitJoin = 0
  FixShape = 1
  InnerFit = 0
  InnerFitJoin = 0
  InvalidShape = false
  Linearize = true
  NewSolid = false
  Profile = -> Sketch263
  ReferenceAxis = -> Sketch263 [H_Axis]
  Refine = true
  Suppress = false
  TreeRank = 179
  ValidateShape = true
  _ProfileBasedVersion = 1
FEATURE [PartDesign::Chamfer] Chamfer061
  AddSubType = 0
  Angle = 45
  Base = -> Revolution027 [Edge5,Edge3]
  BaseFeature = -> Revolution027
  ChamferType = 0
  FixShape = 1
  FlipDirection = false
  InvalidShape = false
  NewSolid = false
  Refine = true
  Size = 0.2
  Size2 = 1
  SupportTransform = false
  Suppress = false
  TreeRank = 180
  UseAllEdges = false
  ValidateShape = true
FEATURE [PartDesign::Chamfer] Chamfer062
  AddSubType = 0
  Angle = 45
  Base = -> Chamfer061 [Edge6]
  BaseFeature = -> Chamfer061
  ChamferType = 0
  FixShape = 1
  FlipDirection = false
  InvalidShape = false
  NewSolid = false
  Refine = true
  Size = 0.2
  Size2 = 1
  SupportTransform = false
  Suppress = false
  TreeRank = 181
  UseAllEdges = false
  ValidateShape = true
FEATURE [PartDesign::Fillet] Fillet053
  AddSubType = 0
  Base = -> Chamfer062 [Edge39,Edge35,Edge43,Edge41,Edge37,Edge34]
  BaseFeature = -> Chamfer062
  FixShape = 1
  InvalidShape = false
  NewSolid = false
  Radius = 0.4
  Refine = true
  SupportTransform = false
  Suppress = false
  TreeRank = 182
  UseAllEdges = false
  ValidateShape = true
FEATURE [PartDesign::Body] Body123  label="Tube-connector-M5-ID5mm"
  AutoGroupSolids = false
  ClaimAllChildren = false
  ExportMode = 0
  FixShape = 1
  Group = -> [Sketch261,Pad104,Sketch262,Revolution026,Sketch263,Revolution027,Chamfer061,Chamfer062,Fillet053]
  InvalidShape = false
  Origin = -> Origin227
  Placement = pos=(6.7,0,4) rot=(0,0,1;0rad)
  SingleSolid = true
  Tip = -> Fillet053
  TreeRank = 170
  ValidateShape = false
  _ExportChildren = -> [Pad104,Revolution026,Revolution027,Chamfer061,Chamfer062,Fillet053]
  _GroupVersion = 1
FEATURE [Sketcher::SketchObject] Sketch264
  ArcFitTolerance = 1e-06
  AttachmentSupport = -> [YZ_Plane150]
  ExternalBSplineMaxDegree = 5
  ExternalBSplineTolerance = 0.0001
  FixShape = 1
  FullyConstrained = true
  InternalTolerance = 1e-06
  InvalidShape = false
  MakeInternals = false
  MapMode = 5
  Placement = pos=(0,0,0) rot=(0.57735,0.57735,0.57735;2.0944rad)
  Support = -> [YZ_Plane150]
  TreeRank = 194
  ValidateShape = false
  sketch-geometry (2):
    g0: Circle CenterX=0 CenterY=0 CenterZ=0 NormalX=0 NormalY=0 NormalZ=1 AngleXU=0 Radius=2.5
    g1: Circle CenterX=0 CenterY=0 CenterZ=0 NormalX=0 NormalY=0 NormalZ=1 AngleXU=0 Radius=4
  constraints (4):
    c: Coincident(g0,g-1)
    c: Coincident(g1,g0)
    c: Diameter(g0) = 5
    c: Diameter(g1) = 8
FEATURE [PartDesign::Pad] Pad105
  AddSubType = 0
  AlongSketchNormal = false
  AutoTaperInnerAngle = true
  CheckUpToFaceLimits = true
  ClaimChildren = false
  Direction = (1,-2e-16,3e-16)
  Fit = 0
  FitJoin = 0
  FixShape = 1
  InnerFit = 0
  InnerFitJoin = 0
  InvalidShape = false
  Length = 0.7
  Length2 = 10
  Linearize = true
  NewSolid = false
  Profile = -> Sketch264
  ReferenceAxis = -> Sketch264 [N_Axis]
  Refine = true
  Suppress = false
  TaperInnerAngle = 0
  TaperInnerAngleRev = 0
  TreeRank = 195
  Type = 0
  ValidateShape = true
  _ProfileBasedVersion = 1
FEATURE [PartDesign::Body] Body124  label="Rondelle"
  AutoGroupSolids = false
  ClaimAllChildren = false
  ExportMode = 0
  FixShape = 1
  Group = -> [Sketch264,Pad105]
  InvalidShape = false
  Origin = -> Origin229
  Placement = pos=(6,0,4) rot=(0,0,1;0rad)
  SingleSolid = true
  Tip = -> Pad105
  TreeRank = 193
  ValidateShape = false
  _ExportChildren = -> [Pad105]
  _GroupVersion = 1
PROVENANCE & LICENSES
A FreeCAD (.FCStd) document from a public repository crawl; recipes are the document's own serialized feature recipes (and, for linked parts, companion documents' recipes).
License: as declared in the source repository (recorded in the dataset sidecar).
